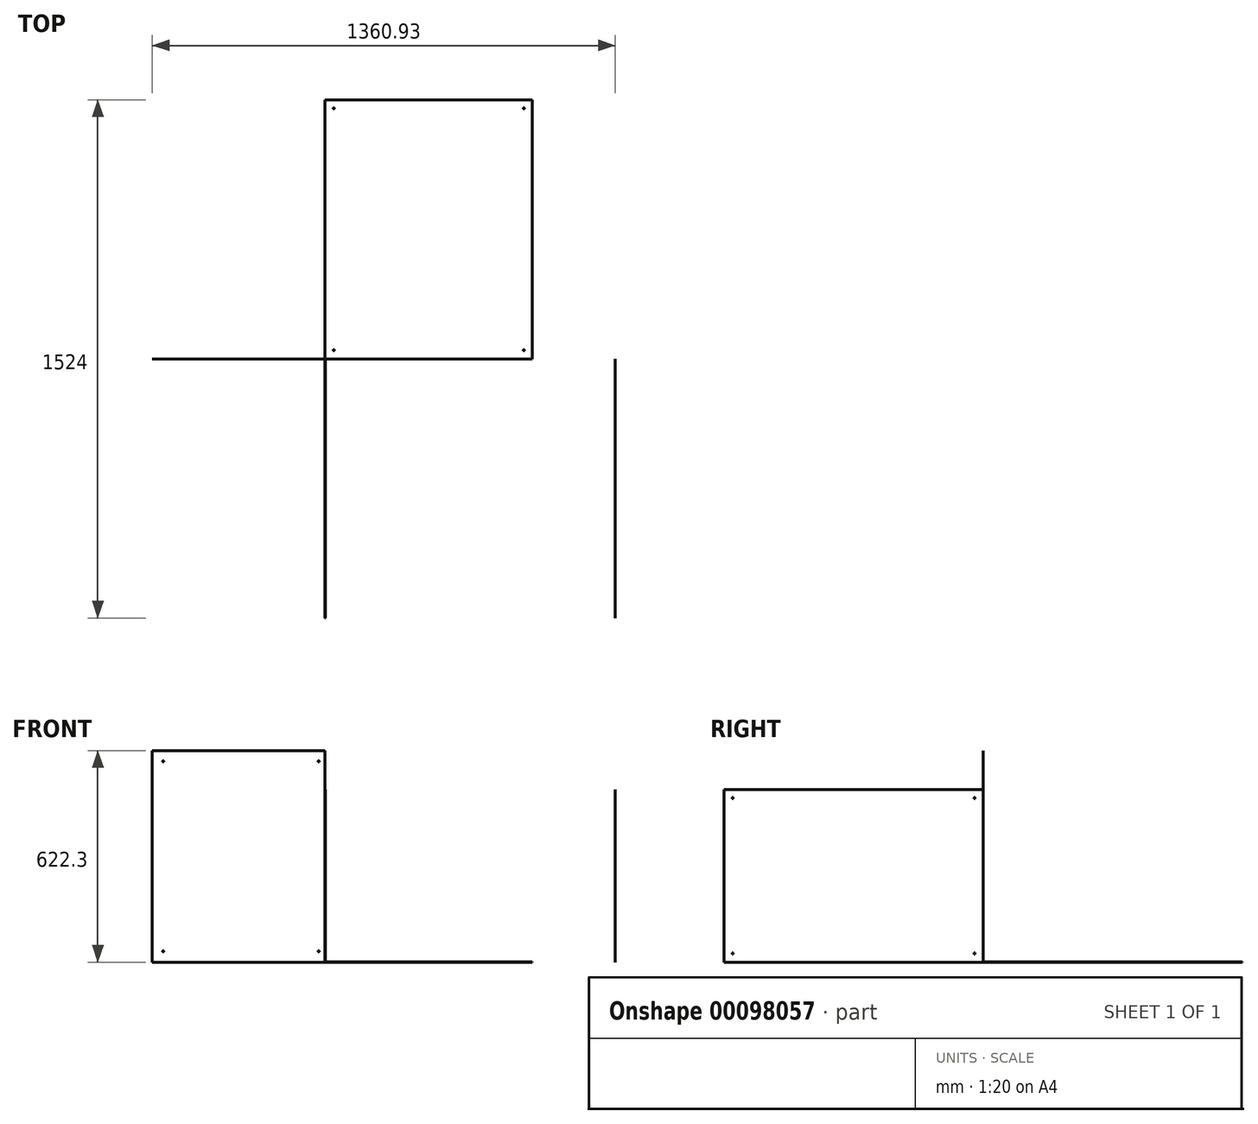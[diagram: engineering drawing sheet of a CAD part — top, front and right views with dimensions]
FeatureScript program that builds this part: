
annotation { "Feature Type Name" : "Feature", "Feature Type Description" : "" }
export const myFeature = defineFeature(function(context is Context, id is Id, definition is map)
    precondition{}
    {
        {
            var Q0;
            Q0=qCreatedBy(makeId("Top.planeOp"),FACE);
            var sketch = newSketch(context, id + "F0", { "sketchPlane" : qUnion([Q0])});
            skLineSegment(sketch, "E0.bottom", {"start": v(0, 0) * mm, "end": v(609.6, 0) * mm});
            skLineSegment(sketch, "E0.top", {"start": v(0, 762) * mm, "end": v(609.6, 762) * mm});
            skLineSegment(sketch, "E0.left", {"start": v(0, 0) * mm, "end": v(0, 762) * mm});
            skLineSegment(sketch, "E0.right", {"start": v(609.6, 0) * mm, "end": v(609.6, 762) * mm});
            skSolve(sketch);
        }
        {
            var Q0;
            Q0=makeQuery(id+"F0.imprint","IMPRINT",FACE,{"disambiguationData":[TD([[makeQuery(id+"F0.imprint","IMPRINT",EDGE,{"derivedFrom":sQuery(id+"F0.wireOp",EDGE,"E0.bottom")}),1.0]])]});
            var sketch = newSketch(context, id + "F1", { "sketchPlane" : qUnion([Q0])});
            skLineSegment(sketch, "E1", {"start": v(0, 0) * mm, "end": v(25.4, 0) * mm, "construction": true});
            skLineSegment(sketch, "E2", {"start": v(25.4, 0) * mm, "end": v(25.4, 25.4) * mm, "construction": true});
            skCircle(sketch, "E3", {"center": v(25.4, 25.4) * mm, "radius": 1.59 * mm});
            skCircle(sketch, "E4.0.1.0", {"center": v(25.4, 736.6) * mm, "radius": 1.59 * mm});
            skCircle(sketch, "E4.1.0.0", {"center": v(584.2, 25.4) * mm, "radius": 1.59 * mm});
            skCircle(sketch, "E4.1.1.0", {"center": v(584.2, 736.6) * mm, "radius": 1.59 * mm});
            skCircle(sketch, "E4.2.0.0", {"center": v(1143, 25.4) * mm, "radius": 1.59 * mm});
            skCircle(sketch, "E4.2.1.0", {"center": v(1143, 736.6) * mm, "radius": 1.59 * mm});
            skLineSegment(sketch, "E4.direction1", {"start": v(25.4, 25.4) * mm, "end": v(584.2, 25.4) * mm, "construction": true});
            skLineSegment(sketch, "E4.direction2", {"start": v(25.4, 25.4) * mm, "end": v(25.4, 736.6) * mm, "construction": true});
            skSolve(sketch);
        }
        {
            assignVariable(context, id + "F2", {"name" : "Thickness", "anyValue" : 0.25});
        }
        {
            var Q0;
            Q0=makeQuery(id+"F1.imprint","IMPRINT",FACE,{"disambiguationData":[TD([[makeQuery(id+"F1.imprint","IMPRINT",EDGE,{"derivedFrom":sQuery(id+"F1.wireOp",EDGE,"E3")}),-1.0]])]});
            extrude(context, id + "F3", {"entities" : qUnion([Q0]), "depth" : (getVariable(context, 'Thickness')) * mm});
        }
        {
            var Q0;
            Q0=qCreatedBy(makeId("Right.planeOp"),FACE);
            var sketch = newSketch(context, id + "F4", { "sketchPlane" : qUnion([Q0])});
            skLineSegment(sketch, "E5.bottom", {"start": v(0, 0) * mm, "end": v(-762, 0) * mm});
            skLineSegment(sketch, "E5.top", {"start": v(0, 508) * mm, "end": v(-762, 508) * mm});
            skLineSegment(sketch, "E5.left", {"start": v(0, 0) * mm, "end": v(0, 508) * mm});
            skLineSegment(sketch, "E5.right", {"start": v(-762, 0) * mm, "end": v(-762, 508) * mm});
            skSolve(sketch);
        }
        {
            var Q0;
            Q0=makeQuery(id+"F4.imprint","IMPRINT",FACE,{"disambiguationData":[TD([[makeQuery(id+"F4.imprint","IMPRINT",EDGE,{"derivedFrom":sQuery(id+"F4.wireOp",EDGE,"E5.bottom")}),-1.0]])]});
            var sketch = newSketch(context, id + "F5", { "sketchPlane" : qUnion([Q0])});
            skLineSegment(sketch, "E6", {"start": v(0, 0) * mm, "end": v(-25.4, 0) * mm, "construction": true});
            skLineSegment(sketch, "E7", {"start": v(-25.4, 0) * mm, "end": v(-25.4, 25.4) * mm, "construction": true});
            skCircle(sketch, "E8", {"center": v(-25.4, 25.4) * mm, "radius": 1.59 * mm});
            skCircle(sketch, "E9.0.1.0", {"center": v(-25.4, 482.6) * mm, "radius": 1.59 * mm});
            skCircle(sketch, "E9.1.0.0", {"center": v(-736.6, 25.4) * mm, "radius": 1.59 * mm});
            skCircle(sketch, "E9.1.1.0", {"center": v(-736.6, 482.6) * mm, "radius": 1.59 * mm});
            skCircle(sketch, "E9.2.0.0", {"center": v(-1447.8, 25.4) * mm, "radius": 1.59 * mm});
            skCircle(sketch, "E9.2.1.0", {"center": v(-1447.8, 482.6) * mm, "radius": 1.59 * mm});
            skLineSegment(sketch, "E9.direction1", {"start": v(-25.4, 25.4) * mm, "end": v(-736.6, 25.4) * mm, "construction": true});
            skLineSegment(sketch, "E9.direction2", {"start": v(-25.4, 25.4) * mm, "end": v(-25.4, 482.6) * mm, "construction": true});
            skSolve(sketch);
        }
        {
            var Q0;
            Q0=makeQuery(id+"F5.imprint","IMPRINT",FACE,{"disambiguationData":[TD([[makeQuery(id+"F5.imprint","IMPRINT",EDGE,{"derivedFrom":sQuery(id+"F5.wireOp",EDGE,"E8")}),-1.0]])]});
            extrude(context, id + "F6", {"entities" : qUnion([Q0]), "depth" : (getVariable(context, 'Thickness')) * mm});
        }
        {
            var Q0;
            Q0=makeQuery(id+"F6.opExtrude","SWEPT_BODY",BODY,{"disambiguationData":[OSD([sQuery(id+"F4.wireOp",EDGE,"E5.bottom"),sQuery(id+"F4.wireOp",EDGE,"E5.top"),sQuery(id+"F4.wireOp",EDGE,"E5.left"),sQuery(id+"F4.wireOp",EDGE,"E5.right"),sQuery(id+"F5.wireOp",EDGE,"E8"),sQuery(id+"F5.wireOp",EDGE,"E9.0.1.0"),sQuery(id+"F5.wireOp",EDGE,"E9.1.0.0"),sQuery(id+"F5.wireOp",EDGE,"E9.1.1.0")])]});
            transform(context, id + "F7", {"entities" : qUnion([Q0]), "transformType" : TransformType.TRANSLATION_3D, "dx" : 852.68 * mm, "dy" : 0 * mm, "dz" : 0 * mm, "makeCopy" : true});
        }
        {
            var Q0;
            Q0=qCreatedBy(makeId("Front.planeOp"),FACE);
            var sketch = newSketch(context, id + "F8", { "sketchPlane" : qUnion([Q0])});
            skLineSegment(sketch, "E10.bottom", {"start": v(0, 0) * mm, "end": v(-508, 0) * mm});
            skLineSegment(sketch, "E10.top", {"start": v(0, 622.3) * mm, "end": v(-508, 622.3) * mm});
            skLineSegment(sketch, "E10.left", {"start": v(0, 0) * mm, "end": v(0, 622.3) * mm});
            skLineSegment(sketch, "E10.right", {"start": v(-508, 0) * mm, "end": v(-508, 622.3) * mm});
            skLineSegment(sketch, "E11", {"start": v(-508, 0) * mm, "end": v(-508, 31.75) * mm, "construction": true});
            skLineSegment(sketch, "E12", {"start": v(-508, 31.75) * mm, "end": v(-476.25, 31.75) * mm, "construction": true});
            skLineSegment(sketch, "E13", {"start": v(-508, 31.75) * mm, "end": v(-508, 0) * mm, "construction": true});
            skCircle(sketch, "E14", {"center": v(-476.25, 31.75) * mm, "radius": 1.59 * mm});
            skCircle(sketch, "E15.0.1.0", {"center": v(-476.25, 590.55) * mm, "radius": 1.59 * mm});
            skCircle(sketch, "E15.1.0.0", {"center": v(-19.05, 31.75) * mm, "radius": 1.59 * mm});
            skCircle(sketch, "E15.1.1.0", {"center": v(-19.05, 590.55) * mm, "radius": 1.59 * mm});
            skCircle(sketch, "E15.2.0.0", {"center": v(438.15, 31.75) * mm, "radius": 1.59 * mm});
            skCircle(sketch, "E15.2.1.0", {"center": v(438.15, 590.55) * mm, "radius": 1.59 * mm});
            skLineSegment(sketch, "E15.direction1", {"start": v(-476.25, 31.75) * mm, "end": v(-19.05, 31.75) * mm, "construction": true});
            skLineSegment(sketch, "E15.direction2", {"start": v(-476.25, 31.75) * mm, "end": v(-476.25, 590.55) * mm, "construction": true});
            skSolve(sketch);
        }
        {
            var Q0;
            Q0=makeQuery(id+"F8.imprint","IMPRINT",FACE,{"disambiguationData":[TD([[makeQuery(id+"F8.imprint","IMPRINT",EDGE,{"derivedFrom":sQuery(id+"F8.wireOp",EDGE,"E10.bottom")}),-1.0]])]});
            extrude(context, id + "F9", {"entities" : qUnion([Q0]), "depth" : (getVariable(context, 'Thickness')) * mm});
        }
    });
